# Revit family: FU_Config_Sandler_Kern 0310
name_source: partatom
category: Furniture
units: mm (PartAtom-declared; Revit-internal decimal feet)

## family parameters
Always vertical = Yes
Cut with Voids When Loaded = No
OmniClass Number = 23.40.20.00
OmniClass Title = General Furniture and Specialties
Render Appearance Source = Family Geometry
Room Calculation Point = No
Shared = No
Work Plane-Based = No

## types (1)
- Kern 3010
    Default Elevation = 0 mm  [stored 0 ft]
    Depth = 1620 mm  [stored 5.31496 ft]
    Description = Room Configuration 1: a four-seat room consisting of 2 two-seat sofas (KER0030), 2 rear privacy screens (KER1030PC), and 1 wide connecting panel (KER2120). 102.4"/260cm wide, 63"/160cm deep.
    Frame = Epoxy - M1_B00 - Black
    Height = 1260 mm  [stored 4.13386 ft]
    Manufacturer = Sandler
    Model = Kern 3010
    URL = https://www.sandlerseating.com
    Width = 2570 mm  [stored 8.43176 ft]

note: [stored X ft] marks values corroborated as IEEE doubles in the binary element streams (Revit-internal decimal feet)

## geometry (parser evidence)
native form markers: Sweep x16
no freeform markers — native parametric forms only
